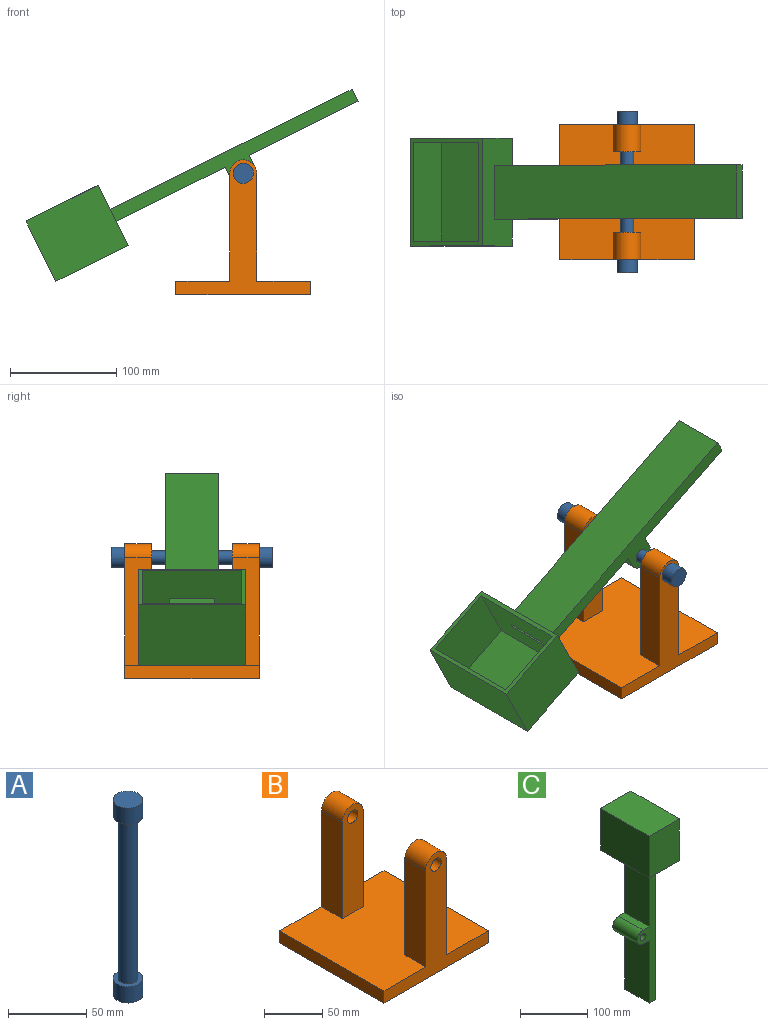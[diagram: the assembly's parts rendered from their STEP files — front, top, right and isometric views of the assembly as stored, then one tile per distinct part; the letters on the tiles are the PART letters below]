
ASSEMBLY  parts=3 mates=2
PART A: 7 faces, bbox 19.1x19.1x152.4 mm
  f0: cylinder r=6.35mm len=127mm, axis (0,0,-1), area 5067.1mm2, adj f3,f6
  f1: cylinder r=9.53mm len=19.05mm, axis (0,0,-1), area 760.1mm2, adj f2,f3
  f2: plane 19.05x19.05mm, normal (0,0,1), area 285mm2, adj f1
  f3: plane 19.05x19.05mm, normal (0,0,-1), area 158.3mm2, adj f0,f1
  f4: cylinder r=9.53mm len=19.05mm, axis (0,0,1), area 760.1mm2, adj f5,f6
  f5: plane 19.05x19.05mm, normal (0,0,-1), area 285mm2, adj f4
  f6: plane 19.05x19.05mm, normal (0,0,1), area 158.3mm2, adj f0,f4
PART B: 16 faces, bbox 127x127x127 mm
  f0: plane 127x127mm, normal (0,0,1), area 14838.7mm2, adj f1,f2,f3,f4,f6,f7,f8,f9
  f1: plane 127x12.7mm, normal (-1,0,0), area 1612.9mm2, adj f0,f2,f4,f5
  f2: plane 127x127mm, normal (0,-1,0), area 4320.2mm2, adj f0,f1,f3,f5,f6,f7,f12,f15
  f3: plane 127x12.7mm, normal (1,0,0), area 1612.9mm2, adj f0,f2,f4,f5
  f4: plane 127x127mm, normal (0,1,0), area 4320.2mm2, adj f0,f1,f3,f5,f9,f10,f13,f14
  f5: plane 127x127mm, normal (0,0,-1), area 16129mm2, adj f1,f2,f3,f4
  f6: plane 101.6x25.4mm, normal (-1,0,0), area 2580.6mm2, adj f0,f2,f8,f12
  f7: plane 101.6x25.4mm, normal (1,0,0), area 2580.6mm2, adj f0,f2,f8,f12
  f8: plane 114.3x25.4mm, normal (0,1,0), area 2707.3mm2, adj f0,f6,f7,f12,f15
  f9: plane 101.6x25.4mm, normal (1,0,0), area 2580.6mm2, adj f0,f4,f11,f13
  f10: plane 101.6x25.4mm, normal (-1,0,0), area 2580.6mm2, adj f0,f4,f11,f13
  f11: plane 114.3x25.4mm, normal (0,-1,0), area 2707.3mm2, adj f0,f9,f10,f13,f14
  f12: cylinder r=12.7mm len=25.4mm, axis (0,-1,0), area 1013.4mm2, adj f2,f6,f7,f8
  f13: cylinder r=12.7mm len=25.4mm, axis (0,-1,0), area 1013.4mm2, adj f4,f9,f10,f11
  f14: cylinder r=6.35mm len=25.4mm, axis (0,-1,0), area 1013.4mm2, adj f4,f11
  f15: cylinder r=6.35mm len=25.4mm, axis (0,-1,0), area 1013.4mm2, adj f2,f8
PART C: 26 faces, bbox 63.5x101.6x330.2 mm
  f0: plane 114.3x50.8mm, normal (-1,0,0), area 5806.4mm2, adj f2,f4,f6,f22
  f1: plane 101.6x76.2mm, normal (1,0,0), area 1296.8mm2, adj f8,f9,f10,f11,f18,f19,f20,f21
  f2: plane 254x38.1mm, normal (0,-1,0), area 3675.1mm2, adj f0,f3,f5,f6,f11,f22,f23,f24
  f3: plane 254x50.8mm, normal (1,0,0), area 12903.2mm2, adj f2,f4,f6,f11
  f4: plane 254x38.1mm, normal (0,1,0), area 3675.1mm2, adj f0,f3,f5,f6,f11,f22,f23,f24
  f5: plane 114.3x50.8mm, normal (-1,0,0), area 5806.4mm2, adj f2,f4,f11,f23
  f6: plane 50.8x12.7mm, normal (0,0,-1), area 645.2mm2, adj f0,f2,f3,f4
  f7: plane 101.6x76.2mm, normal (-1,0,0), area 7741.9mm2, adj f8,f9,f10,f11
  f8: plane 76.2x63.5mm, normal (0,-1,0), area 4838.7mm2, adj f1,f7,f10,f11
  f9: plane 76.2x63.5mm, normal (0,1,0), area 4838.7mm2, adj f1,f7,f10,f11
  f10: plane 101.6x63.5mm, normal (0,0,1), area 6451.6mm2, adj f1,f7,f8,f9
  f11: plane 101.6x63.5mm, normal (0,0,-1), area 5806.4mm2, adj f1,f2,f3,f4,f5,f7,f8,f9
  f12: plane 254x5.08mm, normal (0,1,0), area 1290.3mm2, adj f13,f15,f16,f21
  f13: plane 254x43.18mm, normal (-1,0,0), area 10967.7mm2, adj f12,f14,f16,f21
  f14: plane 254x5.08mm, normal (0,-1,0), area 1290.3mm2, adj f13,f15,f16,f21
  f15: plane 254x43.18mm, normal (1,0,0), area 10967.7mm2, adj f12,f14,f16,f21
  f16: plane 43.18x5.08mm, normal (0,0,1), area 219.4mm2, adj f12,f13,f14,f15
  f17: plane 93.98x68.58mm, normal (1,0,0), area 6445.1mm2, adj f18,f19,f20,f21
  f18: plane 68.58x59.69mm, normal (0,1,0), area 4093.5mm2, adj f1,f17,f20,f21
  f19: plane 68.58x59.69mm, normal (0,-1,0), area 4093.5mm2, adj f1,f17,f20,f21
  f20: plane 93.98x59.69mm, normal (0,0,-1), area 5609.7mm2, adj f1,f17,f18,f19
  f21: plane 93.98x59.69mm, normal (0,0,1), area 5390.3mm2, adj f1,f12,f13,f14,f15,f17,f18,f19
  f22: plane 50.8x12.7mm, normal (0,0,-1), area 645.2mm2, adj f0,f2,f4,f24
  f23: plane 50.8x12.7mm, normal (0,0,1), area 645.2mm2, adj f2,f4,f5,f24
  f24: cylinder r=12.7mm len=50.8mm, axis (0,-1,0), area 2026.8mm2, adj f2,f4,f22,f23
  f25: cylinder r=6.35mm len=50.8mm, axis (0,-1,0), area 2026.8mm2, adj f2,f4
PLACE A rot(axis=(-0.79,-0.43,-0.43),103.1deg) t=(-417.06,-67.78,236.22)mm
PLACE B t=(-176.54,-12.84,-35.24)mm fixed
PLACE C rot(axis=(0,-1,0),116.4deg) t=(-64.45,452.83,141.32)mm
MATE revolute C.f24 <-> A.f0  axis (0,-1,0) through (-175.33,-4.28,79.06)mm
MATE revolute A.f0 <-> B.f12  axis (0,-1,0) through (-175.33,-67.78,79.06)mm
